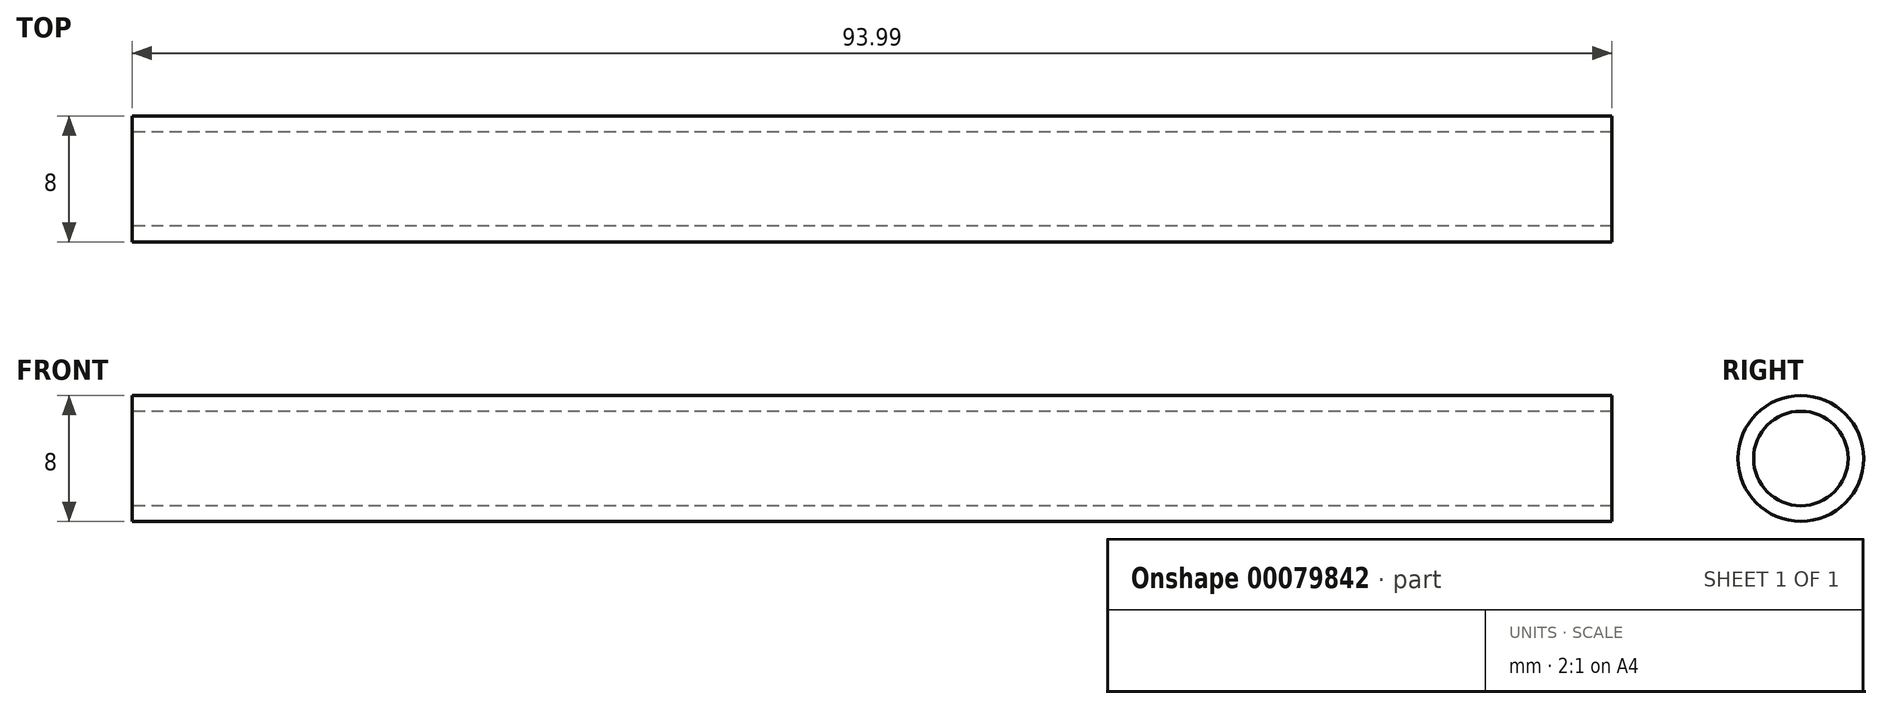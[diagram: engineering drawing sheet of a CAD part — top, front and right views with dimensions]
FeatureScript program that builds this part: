
annotation { "Feature Type Name" : "Feature", "Feature Type Description" : "" }
export const myFeature = defineFeature(function(context is Context, id is Id, definition is map)
    precondition{}
    {
        {
            var Q0;
            Q0=qCreatedBy(makeId("Front.planeOp"),FACE);
            var sketch = newSketch(context, id + "F0", { "sketchPlane" : qUnion([Q0])});
            skLineSegment(sketch, "E0", {"start": v(0, 0) * mm, "end": v(94, 0) * mm});
            skLineSegment(sketch, "E1", {"start": v(0, 0) * mm, "end": v(0, 4) * mm});
            skLineSegment(sketch, "E2", {"start": v(94, 0) * mm, "end": v(93.99, 4) * mm});
            skLineSegment(sketch, "E3", {"start": v(0, 4) * mm, "end": v(93.99, 4) * mm});
            skSolve(sketch);
        }
        {
            var Q0;
            Q0=qCreatedBy(makeId("Front.planeOp"),FACE);
            var sketch = newSketch(context, id + "F2", { "sketchPlane" : qUnion([Q0])});
            skLineSegment(sketch, "E4", {"start": v(-47.75, 0) * mm, "end": v(127.43, 0) * mm});
            skSolve(sketch);
        }
        {
            var Q0;
            Q0=qSketchRegion(id+"F0",true);
            var Q1;
            Q1=qBodyType(qCreatedBy(id+"F2",EDGE),BodyType.WIRE);
            revolve(context, id + "F3", {"entities" : qUnion([Q0]), "axis" : qUnion([Q1]), "revolveType" : RevolveType.FULL});
        }
        {
            var Q0;
            Q0=makeQuery(id+"F3.opRevolve","SWEPT_FACE",FACE,{"disambiguationData":[OSD([sQuery(id+"F0.wireOp",EDGE,"E2")])]});
            var Q1;
            Q1=makeQuery(id+"F3.opRevolve","SWEPT_FACE",FACE,{"disambiguationData":[OSD([sQuery(id+"F0.wireOp",EDGE,"E1")])]});
            shell(context, id + "F1", {"entities" : qUnion([Q0, Q1]), "thickness" : 1 * mm});
        }
    });
